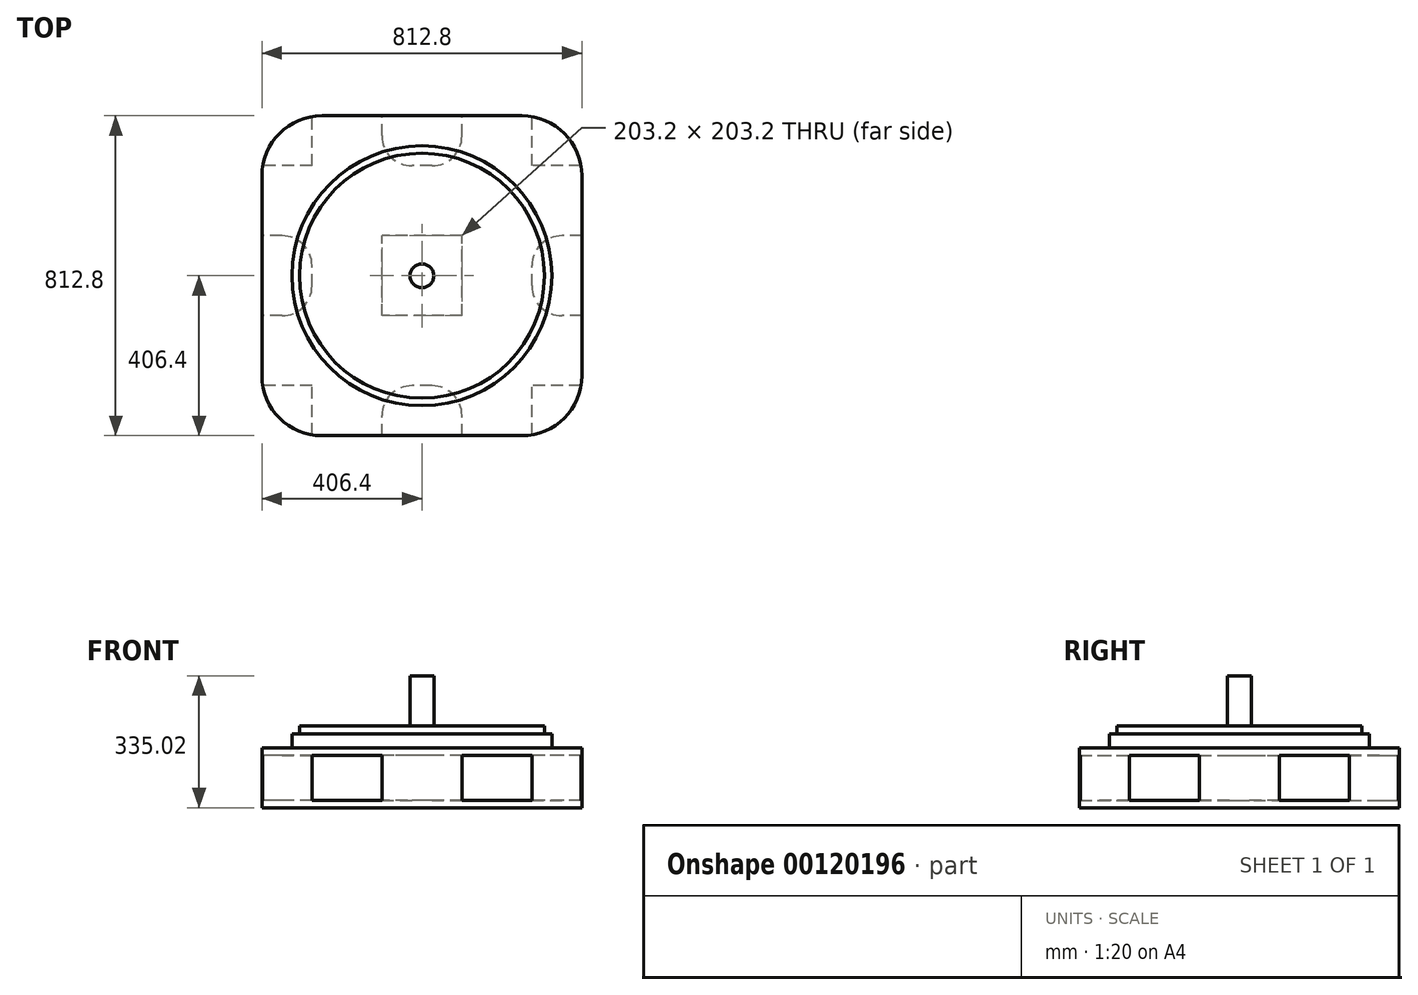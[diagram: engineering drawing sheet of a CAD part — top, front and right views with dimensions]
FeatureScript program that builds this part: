
annotation { "Feature Type Name" : "Feature", "Feature Type Description" : "" }
export const myFeature = defineFeature(function(context is Context, id is Id, definition is map)
    precondition{}
    {
        {
            var Q0;
            Q0=qCreatedBy(makeId("Top.planeOp"),FACE);
            var sketch = newSketch(context, id + "F0", { "sketchPlane" : qUnion([Q0])});
            skCircle(sketch, "E0", {"center": v(0, 0) * mm, "radius": 311.15 * mm});
            skSolve(sketch);
        }
        {
            var Q0;
            Q0 = qSketchRegion(id + "F0", true);
            extrude(context, id + "F1", {"entities" : qUnion([Q0]), "depth" : 20.57 * mm});
        }
        {
            var Q0;
            Q0=makeQuery(id+"F1.opExtrude","CAP_FACE",FACE,{"disambiguationData":[OSD([sQuery(id+"F0.wireOp",EDGE,"E0")])],"isStart":true});
            var sketch = newSketch(context, id + "F2", { "sketchPlane" : qUnion([Q0])});
            skCircle(sketch, "E1", {"center": v(0, 0) * mm, "radius": 330.2 * mm});
            skSolve(sketch);
        }
        {
            var Q0;
            Q0 = qSketchRegion(id + "F2", true);
            extrude(context, id + "F3", {"entities" : qUnion([Q0]), "operationType" : NewBodyOperationType.ADD, "depth" : 35.05 * mm});
        }
        {
            var Q0;
            Q0=makeQuery(id+"F3.opExtrude","CAP_FACE",FACE,{"disambiguationData":[OSD([sQuery(id+"F2.wireOp",EDGE,"E1")])],"isStart":false});
            var sketch = newSketch(context, id + "F4", { "sketchPlane" : qUnion([Q0])});
            skLineSegment(sketch, "E2.bottom", {"start": v(406.4, 406.4) * mm, "end": v(-406.4, 406.4) * mm});
            skLineSegment(sketch, "E2.top", {"start": v(406.4, -406.4) * mm, "end": v(-406.4, -406.4) * mm});
            skLineSegment(sketch, "E2.left", {"start": v(406.4, 406.4) * mm, "end": v(406.4, -406.4) * mm});
            skLineSegment(sketch, "E2.right", {"start": v(-406.4, 406.4) * mm, "end": v(-406.4, -406.4) * mm});
            skPoint(sketch, "E2.middle", {"position": v(0, 0) * mm});
            skSolve(sketch);
        }
        {
            var Q0;
            Q0 = qSketchRegion(id + "F4", true);
            extrude(context, id + "F5", {"entities" : qUnion([Q0]), "operationType" : NewBodyOperationType.ADD, "depth" : 152.4 * mm});
        }
        {
            var Q0;
            Q0=makeQuery(id+"F5.opExtrude","SWEPT_FACE",FACE,{"disambiguationData":[OSD([sQuery(id+"F4.wireOp",EDGE,"E2.top")])]});
            var sketch = newSketch(context, id + "F6", { "sketchPlane" : qUnion([Q0])});
            skLineSegment(sketch, "E3.bottom", {"start": v(279.4, -168.4) * mm, "end": v(101.6, -168.4) * mm});
            skLineSegment(sketch, "E3.top", {"start": v(279.4, -54.1) * mm, "end": v(101.6, -54.1) * mm});
            skLineSegment(sketch, "E3.left", {"start": v(279.4, -168.4) * mm, "end": v(279.4, -54.1) * mm});
            skLineSegment(sketch, "E3.right", {"start": v(101.6, -168.4) * mm, "end": v(101.6, -54.1) * mm});
            skPoint(sketch, "E3.middle", {"position": v(190.5, -111.25) * mm});
            skPoint(sketch, "E3.middle.positionSnap0", {"position": v(406.4, -111.25) * mm});
            skPoint(sketch, "E3.centerSnap0", {"position": v(406.4, -111.25) * mm});
            skLineSegment(sketch, "E4.bottom", {"start": v(-279.4, -168.4) * mm, "end": v(-101.6, -168.4) * mm});
            skLineSegment(sketch, "E4.top", {"start": v(-279.4, -54.1) * mm, "end": v(-101.6, -54.1) * mm});
            skLineSegment(sketch, "E4.left", {"start": v(-279.4, -168.4) * mm, "end": v(-279.4, -54.1) * mm});
            skLineSegment(sketch, "E4.right", {"start": v(-101.6, -168.4) * mm, "end": v(-101.6, -54.1) * mm});
            skPoint(sketch, "E4.middle", {"position": v(-190.5, -111.25) * mm});
            skSolve(sketch);
        }
        {
            var Q0;
            Q0 = qSketchRegion(id + "F6", true);
            extrude(context, id + "F7", {"entities" : qUnion([Q0]), "operationType" : NewBodyOperationType.REMOVE, "endBound" : BoundingType.THROUGH_ALL, "oppositeDirection" : true, "depth" : 25.4 * mm});
        }
        {
            var Q0;
            Q0=makeQuery(id+"F5.opExtrude","SWEPT_FACE",FACE,{"disambiguationData":[OSD([sQuery(id+"F4.wireOp",EDGE,"E2.right")])]});
            var sketch = newSketch(context, id + "F8", { "sketchPlane" : qUnion([Q0])});
            skLineSegment(sketch, "E5.bottom", {"start": v(101.6, -168.4) * mm, "end": v(279.4, -168.4) * mm});
            skLineSegment(sketch, "E5.top", {"start": v(101.6, -54.1) * mm, "end": v(279.4, -54.1) * mm});
            skLineSegment(sketch, "E5.left", {"start": v(101.6, -168.4) * mm, "end": v(101.6, -54.1) * mm});
            skLineSegment(sketch, "E5.right", {"start": v(279.4, -168.4) * mm, "end": v(279.4, -54.1) * mm});
            skPoint(sketch, "E5.middle", {"position": v(190.5, -111.25) * mm});
            skPoint(sketch, "E5.middle.positionSnap0", {"position": v(406.4, -111.25) * mm});
            skPoint(sketch, "E5.centerSnap0", {"position": v(406.4, -111.25) * mm});
            skLineSegment(sketch, "E6.bottom", {"start": v(-279.4, -168.4) * mm, "end": v(-101.6, -168.4) * mm});
            skLineSegment(sketch, "E6.top", {"start": v(-279.4, -54.1) * mm, "end": v(-101.6, -54.1) * mm});
            skLineSegment(sketch, "E6.left", {"start": v(-279.4, -168.4) * mm, "end": v(-279.4, -54.1) * mm});
            skLineSegment(sketch, "E6.right", {"start": v(-101.6, -168.4) * mm, "end": v(-101.6, -54.1) * mm});
            skPoint(sketch, "E6.middle", {"position": v(-190.5, -111.25) * mm});
            skPoint(sketch, "E6.middle.positionSnap0", {"position": v(-406.4, -111.25) * mm});
            skPoint(sketch, "E6.centerSnap0", {"position": v(-406.4, -111.25) * mm});
            skSolve(sketch);
        }
        {
            var Q0;
            Q0 = qSketchRegion(id + "F8", true);
            extrude(context, id + "F9", {"entities" : qUnion([Q0]), "operationType" : NewBodyOperationType.REMOVE, "endBound" : BoundingType.THROUGH_ALL, "oppositeDirection" : true, "depth" : 25.4 * mm});
        }
        {
            var Q0;
            Q0=makeQuery(id+"F5.opExtrude","SWEPT_EDGE",EDGE,{"disambiguationData":[OSD([sQuery(id+"F4.wireOp",EDGE,"E2.bottom"),sQuery(id+"F4.wireOp",EDGE,"E2.right")])]});
            var Q1;
            Q1=makeQuery(id+"F5.opExtrude","SWEPT_EDGE",EDGE,{"disambiguationData":[OSD([sQuery(id+"F4.wireOp",EDGE,"E2.top"),sQuery(id+"F4.wireOp",EDGE,"E2.right")])]});
            var Q2;
            Q2=makeQuery(id+"F5.opExtrude","SWEPT_EDGE",EDGE,{"disambiguationData":[OSD([sQuery(id+"F4.wireOp",EDGE,"E2.top"),sQuery(id+"F4.wireOp",EDGE,"E2.left")])]});
            var Q3;
            Q3=makeQuery(id+"F5.opExtrude","SWEPT_EDGE",EDGE,{"disambiguationData":[OSD([sQuery(id+"F4.wireOp",EDGE,"E2.bottom"),sQuery(id+"F4.wireOp",EDGE,"E2.left")])]});
            fillet(context, id + "F10", {"entities" : qUnion([Q0, Q1, Q2, Q3]), "radius" : 152.4 * mm, "tangentPropagation" : true, "allowEdgeOverflow" : false});
        }
        {
            var Q0;
            Q0=makeQuery(id+"F9.boolean.opBoolean","INTERSECT",EDGE,{"derivedFrom":[makeQuery(id+"F7.boolean.opBoolean","COPY",FACE,{"derivedFrom":makeQuery(id+"F7.opExtrude","SWEPT_FACE",FACE,{"disambiguationData":[OSD([sQuery(id+"F6.wireOp",EDGE,"E4.left")])]})}),makeQuery(id+"F9.opExtrude","SWEPT_FACE",FACE,{"disambiguationData":[OSD([sQuery(id+"F8.wireOp",EDGE,"E5.left")])]})]});
            var Q1;
            Q1=makeQuery(id+"F9.boolean.opBoolean","INTERSECT",EDGE,{"derivedFrom":[makeQuery(id+"F7.boolean.opBoolean","COPY",FACE,{"derivedFrom":makeQuery(id+"F7.opExtrude","SWEPT_FACE",FACE,{"disambiguationData":[OSD([sQuery(id+"F6.wireOp",EDGE,"E4.left")])]})}),makeQuery(id+"F9.opExtrude","SWEPT_FACE",FACE,{"disambiguationData":[OSD([sQuery(id+"F8.wireOp",EDGE,"E6.right")])]})]});
            var Q2;
            Q2=makeQuery(id+"F9.boolean.opBoolean","INTERSECT",EDGE,{"derivedFrom":[makeQuery(id+"F7.boolean.opBoolean","COPY",FACE,{"derivedFrom":makeQuery(id+"F7.opExtrude","SWEPT_FACE",FACE,{"disambiguationData":[OSD([sQuery(id+"F6.wireOp",EDGE,"E4.right")])]})}),makeQuery(id+"F9.opExtrude","SWEPT_FACE",FACE,{"disambiguationData":[OSD([sQuery(id+"F8.wireOp",EDGE,"E6.left")])]})]});
            var Q3;
            Q3=makeQuery(id+"F9.boolean.opBoolean","INTERSECT",EDGE,{"derivedFrom":[makeQuery(id+"F7.boolean.opBoolean","COPY",FACE,{"derivedFrom":makeQuery(id+"F7.opExtrude","SWEPT_FACE",FACE,{"disambiguationData":[OSD([sQuery(id+"F6.wireOp",EDGE,"E3.right")])]})}),makeQuery(id+"F9.opExtrude","SWEPT_FACE",FACE,{"disambiguationData":[OSD([sQuery(id+"F8.wireOp",EDGE,"E6.left")])]})]});
            var Q4;
            Q4=makeQuery(id+"F9.boolean.opBoolean","INTERSECT",EDGE,{"derivedFrom":[makeQuery(id+"F7.boolean.opBoolean","COPY",FACE,{"derivedFrom":makeQuery(id+"F7.opExtrude","SWEPT_FACE",FACE,{"disambiguationData":[OSD([sQuery(id+"F6.wireOp",EDGE,"E3.left")])]})}),makeQuery(id+"F9.opExtrude","SWEPT_FACE",FACE,{"disambiguationData":[OSD([sQuery(id+"F8.wireOp",EDGE,"E6.right")])]})]});
            var Q5;
            Q5=makeQuery(id+"F9.boolean.opBoolean","INTERSECT",EDGE,{"derivedFrom":[makeQuery(id+"F7.boolean.opBoolean","COPY",FACE,{"derivedFrom":makeQuery(id+"F7.opExtrude","SWEPT_FACE",FACE,{"disambiguationData":[OSD([sQuery(id+"F6.wireOp",EDGE,"E3.left")])]})}),makeQuery(id+"F9.opExtrude","SWEPT_FACE",FACE,{"disambiguationData":[OSD([sQuery(id+"F8.wireOp",EDGE,"E5.left")])]})]});
            var Q6;
            Q6=makeQuery(id+"F9.boolean.opBoolean","INTERSECT",EDGE,{"derivedFrom":[makeQuery(id+"F7.boolean.opBoolean","COPY",FACE,{"derivedFrom":makeQuery(id+"F7.opExtrude","SWEPT_FACE",FACE,{"disambiguationData":[OSD([sQuery(id+"F6.wireOp",EDGE,"E3.right")])]})}),makeQuery(id+"F9.opExtrude","SWEPT_FACE",FACE,{"disambiguationData":[OSD([sQuery(id+"F8.wireOp",EDGE,"E5.right")])]})]});
            var Q7;
            Q7=makeQuery(id+"F9.boolean.opBoolean","INTERSECT",EDGE,{"derivedFrom":[makeQuery(id+"F7.boolean.opBoolean","COPY",FACE,{"derivedFrom":makeQuery(id+"F7.opExtrude","SWEPT_FACE",FACE,{"disambiguationData":[OSD([sQuery(id+"F6.wireOp",EDGE,"E4.right")])]})}),makeQuery(id+"F9.opExtrude","SWEPT_FACE",FACE,{"disambiguationData":[OSD([sQuery(id+"F8.wireOp",EDGE,"E5.right")])]})]});
            fillet(context, id + "F11", {"entities" : qUnion([Q0, Q1, Q2, Q3, Q4, Q5, Q6, Q7]), "radius" : 76.2 * mm, "tangentPropagation" : true, "allowEdgeOverflow" : false});
        }
        {
            var Q0;
            Q0=makeQuery(id+"F1.opExtrude","CAP_FACE",FACE,{"disambiguationData":[OSD([sQuery(id+"F0.wireOp",EDGE,"E0")])],"isStart":false});
            var sketch = newSketch(context, id + "F12", { "sketchPlane" : qUnion([Q0])});
            skCircle(sketch, "E7", {"center": v(0, 0) * mm, "radius": 30.16 * mm});
            skSolve(sketch);
        }
        {
            var Q0;
            Q0 = qSketchRegion(id + "F12", true);
            extrude(context, id + "F13", {"entities" : qUnion([Q0]), "operationType" : NewBodyOperationType.ADD, "depth" : 127 * mm});
        }
    });
